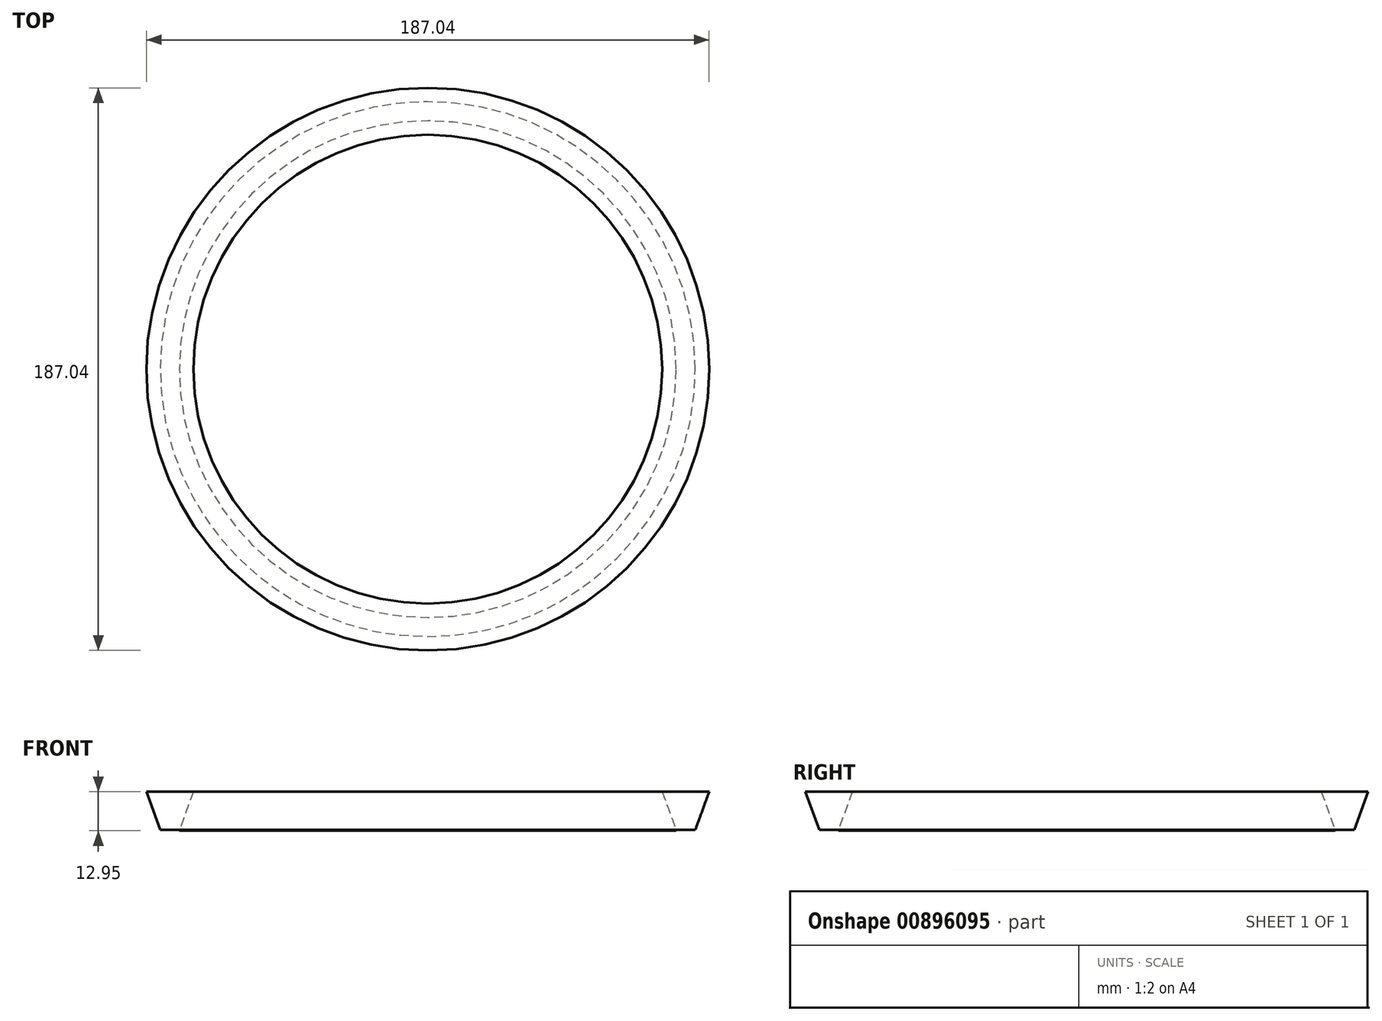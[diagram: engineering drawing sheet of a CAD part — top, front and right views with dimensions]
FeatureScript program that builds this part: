
annotation { "Feature Type Name" : "Feature", "Feature Type Description" : "" }
export const myFeature = defineFeature(function(context is Context, id is Id, definition is map)
    precondition{}
    {
        {
            var Q0;
            Q0=qCreatedBy(makeId("Top.planeOp"),FACE);
            var sketch = newSketch(context, id + "F0", { "sketchPlane" : qUnion([Q0])});
            skCircle(sketch, "E0", {"center": v(0, 0) * mm, "radius": 82.55 * mm});
            skCircle(sketch, "E1", {"center": v(0, 0) * mm, "radius": 88.9 * mm});
            skSolve(sketch);
        }
        {
            var Q0;
            Q0 = qSketchRegion(id + "F0", true);
            var Q1;
            Q1=makeQuery(id+"F0.imprint","IMPRINT",FACE,{"disambiguationData":[TD([[makeQuery(id+"F0.imprint","IMPRINT",EDGE,{"derivedFrom":sQuery(id+"F0.wireOp",EDGE,"E0")}),-1.0]])]});
            extrude(context, id + "F1", {"entities" : qUnion([Q0, Q1]), "depth" : 12.7 * mm, "offsetDistance" : 25.4 * mm, "hasDraft" : true, "draftAngle" : 20 * degree});
        }
        {
            var Q0;
            Q0=makeQuery(id+"F1.opExtrude","CAP_FACE",FACE,{"disambiguationData":[OSD([sQuery(id+"F0.wireOp",EDGE,"E0"),sQuery(id+"F0.wireOp",EDGE,"E1")])],"isStart":true});
            var sketch = newSketch(context, id + "F2", { "sketchPlane" : qUnion([Q0])});
            skCircle(sketch, "E2", {"center": v(0, 0) * mm, "radius": 82.55 * mm});
            skSolve(sketch);
        }
        {
            var Q0;
            Q0 = qSketchRegion(id + "F2", true);
            extrude(context, id + "F3", {"entities" : qUnion([Q0]), "depth" : 0.25 * mm, "offsetDistance" : 25.4 * mm});
        }
    });
